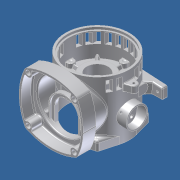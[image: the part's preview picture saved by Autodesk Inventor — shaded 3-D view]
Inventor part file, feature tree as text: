
AUTODESK INVENTOR PART (.ipt)
format: ipt  version: unknown  size: 2,941,952 bytes
history: native  units: in
note: dims shown in document units (in); Inventor stores cm internally (conversion verified against a paired STEP export)
features: extrude x28, sketch x24, plane x15, projected_geometry x10, loft x4, fillet x3, mirror x1, revolve x1, pattern_circular x1, chamfer x1
ambient origin geometry x8: Origin, YZ Plane, XZ Plane, XY Plane, X Axis, Y Axis, Z Axis, Center Point
bodies: Solid1 (feature_tree)
feature tree (88):
  extrude  "Extrusion1"  Depth=2.425in
  extrude  "Extrusion2"  Depth=0.1625in
  plane  "Work Plane3"
  sketch  "Sketch4"  dims[d7=3.375in d8=0.1in]
  plane  "Work Plane4"
  extrude  "Extrusion3"  Depth=0.1in
  sketch  "Sketch6"  dims[d11=0.1in d15=2.6693in]
  extrude  "Extrusion6"  Depth=0.1in
  extrude  "Extrusion7"  Depth=2.6693in
  sketch  "Sketch8"  dims[d19=2.625in d20=0.1in d21=0.0in]
  extrude  "Extrusion8"  Depth=0.575in TaperAngle=0.0deg
  extrude  "Extrusion10"  Depth=0.1in TaperAngle=0.0deg
  plane  "Work Plane5"
  sketch  "Sketch9"  dims[d24=3.15in d25=0.1in]
  extrude  "Extrusion12"  Depth=0.1in
  extrude  "Extrusion13"  Depth=0.1625in
  plane  "Work Plane6"
  extrude  "Extrusion15"  Depth=0.1in TaperAngle=0.0deg
  extrude  "Extrusion16"  Depth=0.5in TaperAngle=0.0deg
  plane  "Work Plane7"
  plane  "Work Plane8"
  plane  "Work Plane9"
  sketch  "Sketch15"  dims[d43=2.725in d44=0.0in d47=2.725in d48=0.0in]
  sketch  "Sketch13"  dims[d35=0.1in d38=0.5in d39=0.0in]
  extrude  "Extrusion19"  Depth=0.1in
  extrude  "Extrusion20"  Depth=2.725in TaperAngle=0.0deg
  plane  "Work Plane11"
  sketch  "Sketch14"  dims[d40=2.725in d41=0.0in d42=0.1in]
  extrude  "Extrusion21"  Depth=1.7in
  plane  "Work Plane12"
  extrude  "Extrusion22"  Depth=0.25in
  mirror  "Mirror3"
  extrude  "Extrusion23"  Depth=2.725in TaperAngle=0.0deg
  plane  "Work Plane15"
  sketch  "Sketch20"  dims[d55=0.0625in d58=2.725in d59=0.0in]
  plane  "Work Plane16"
  plane  "Work Plane17"
  extrude  "Extrusion30"  Depth=0.1in TaperAngle=0.0deg
  extrude  "Extrusion25"  Depth=0.75in
  extrude  "Extrusion26"  Depth=1.185in
  extrude  "Extrusion27"  Depth=0.25in TaperAngle=0.0deg
  extrude  "Extrusion29"  TaperAngle=0.0deg  [1 undecoded]
  extrude  "Extrusion31"  Depth=0.2375in
  extrude  "Extrusion32"  Depth=0.175in
  plane  "Work Plane18"
  extrude  "Extrusion33"  Depth=1.5748in
  plane  "Work Plane19"
  revolve  "Revolution1"  [1 undecoded]
  pattern_circular  "Circular Pattern1"  [2 undecoded]
  extrude  "Extrusion34"  Depth=0.7874in
  extrude  "Extrusion36"  Depth=0.675in
  sketch  "Sketch29"  dims[d83=0.25in d84=0.0in d85=0.2375in]
  plane  "Work Plane20"
  sketch  "Sketch30"  dims[d86=0.55in d87=0.175in]
  loft  "Loft1"
  loft  "Loft2"
  loft  "Loft3"
  loft  "Loft4"
  extrude  "Extrusion37"  Depth=0.4125in
  extrude  "Extrusion38"  Depth=1.0in
  fillet  "Fillet1"  Radius=1.1375in
  fillet  "Fillet3"  Radius=1.25in
  fillet  "Fillet4"  Radius=0.25in
  chamfer  "Chamfer1"  Distance=0.25in
  sketch  "Sketch1"  dims[d0=0.25in d1=2.425in]
  sketch  "Sketch2"  dims[d4=2.425in d5=0.1625in]
  projected_geometry  "Projected Loop1"
  projected_geometry  "Projected Loop2"
  sketch  "Sketch5"  dims[d9=0.1in d10=0.1in]
  sketch  "Sketch7"  dims[d16=2.6693in d17=0.575in d18=0.0in]
  projected_geometry  "Projected Loop3"
  projected_geometry  "Projected Loop4"
  sketch  "Sketch11"  dims[d27=0.25in d29=0.1625in]
  sketch  "Sketch12"  dims[d30=-0.05in d31=0.1in d32=0.0in]
  sketch  "Sketch16"  dims[d49=-0.125in d50=1.7in]
  sketch  "Sketch18"  dims[d51=0.25in d52=0.25in]
  projected_geometry  "Projected Loop6"
  sketch  "Sketch23"  dims[d60=0.175in d61=0.1in d62=0.0in]
  sketch  "Sketch24"  dims[d65=4.0in d66=0.75in]
  projected_geometry  "Projected Loop8"
  sketch  "Sketch25"  dims[d67=0.575in d69=1.185in]
  projected_geometry  "Projected Loop9"
  projected_geometry  "Projected Loop10"
  sketch  "Sketch26"  dims[d71=2.001in d72=0.25in d73=0.0in]
  sketch  "Sketch28"  dims[d81=0.375in d82=0.0in]
  projected_geometry  "Projected Loop12"
  sketch  "Sketch31"  dims[d95=1.5748in d97=0.3625in d98=0.3937in d100=1.0in d102=1.5748in d104=0.3625in d105=0.3937in d107=1.0in d111=0.2375in d112=0.7in d113=0.7874in d115=0.3625in d116=0.3937in d118=1.0in d120=0.675in d121=0.125in d122=0.2375in d123=0.2375in d124=3.05in d127=0.4125in d128=1.0in d129=1.1375in d130=1.25in d131=0.25in d132=0.0in d133=0.25in d134=0.0in d136=-0.5in d139=0.375in d140=0.125in d141=0.375in d142=0.0in d143=1.9175in d147=-0.125in d148=0.635in d149=0.5in d151=0.325in d152=0.375in d153=0.0in d154=0.375in d155=0.0in d156=1.1811in d158=360.0deg d160=0.175in d161=0.275in d167=-1.835in d168=0.1in d169=0.0in d170=1.125in d172=0.25in d173=0.175in d174=0.375in d175=0.175in d177=0.4125in d178=0.0in d179=45.0deg d180=0.175in d181=0.1875in d182=0.0875in d183=0.25in d184=0.0in d185=90.0deg d189=90.0deg d190=0.25in d191=0.175in d192=1.0in d193=0.0in d194=0.075in d195=1.265in d196=0.0in d197=1.265in d198=0.0in d199=1.265in d200=0.0in d201=90.0deg d202=0.175in d203=0.25in d204=1.265in d205=0.0in d206=90.0deg d208=0.175in d209=0.025in d210=90.0deg d211=1.5748in d212=360.0deg d214=0.0625in d216=0.375in d217=1.265in d218=0.0in d221=1.265in d222=0.0in d223=0.0312in d224=0.0312in d225=0.125in d226=0.125in d227=90.0deg d228=2.45in d229=-0.05in d230=0.225in d231=1.5748in d233=360.0deg d235=0.0in d236=90.0deg d237=0.0in d238=90.0deg d239=0.0in d240=90.0deg d241=0.0in d242=90.0deg d243=0.0in d244=90.0deg d245=0.0in d246=90.0deg d247=0.0in d248=90.0deg d249=0.0in d250=90.0deg d251=0.375in d252=0.0in d253=0.125in d254=0.0156in d255=0.125in d256=1.265in d257=0.0in d258=0.025in d259=0.125in d260=45.0deg]
  projected_geometry  "Projected Loop13"
note: 4 required parameter values undecoded (feature->parameter linkage not recoverable at this tier; creation-order binding heuristic only, values carry confidence <= 0.55)